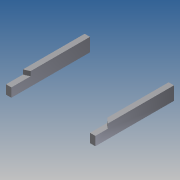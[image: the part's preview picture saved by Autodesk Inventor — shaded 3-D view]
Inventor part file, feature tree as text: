
AUTODESK INVENTOR PART (.ipt)
format: ipt  version: 2014 (Build 180170000, 170)  size: 130,048 bytes
history: native  units: mm
features: extrude x2
ambient origin geometry x8: Origin, YZ Plane, XZ Plane, XY Plane, X Axis, Y Axis, Z Axis, Center Point
bodies: Body1 (feature_tree)
feature tree (2):
  extrude  "Extrusion7"  Depth=1000.0mm
  extrude  "Extrusion8"  Depth=1000.0mm
